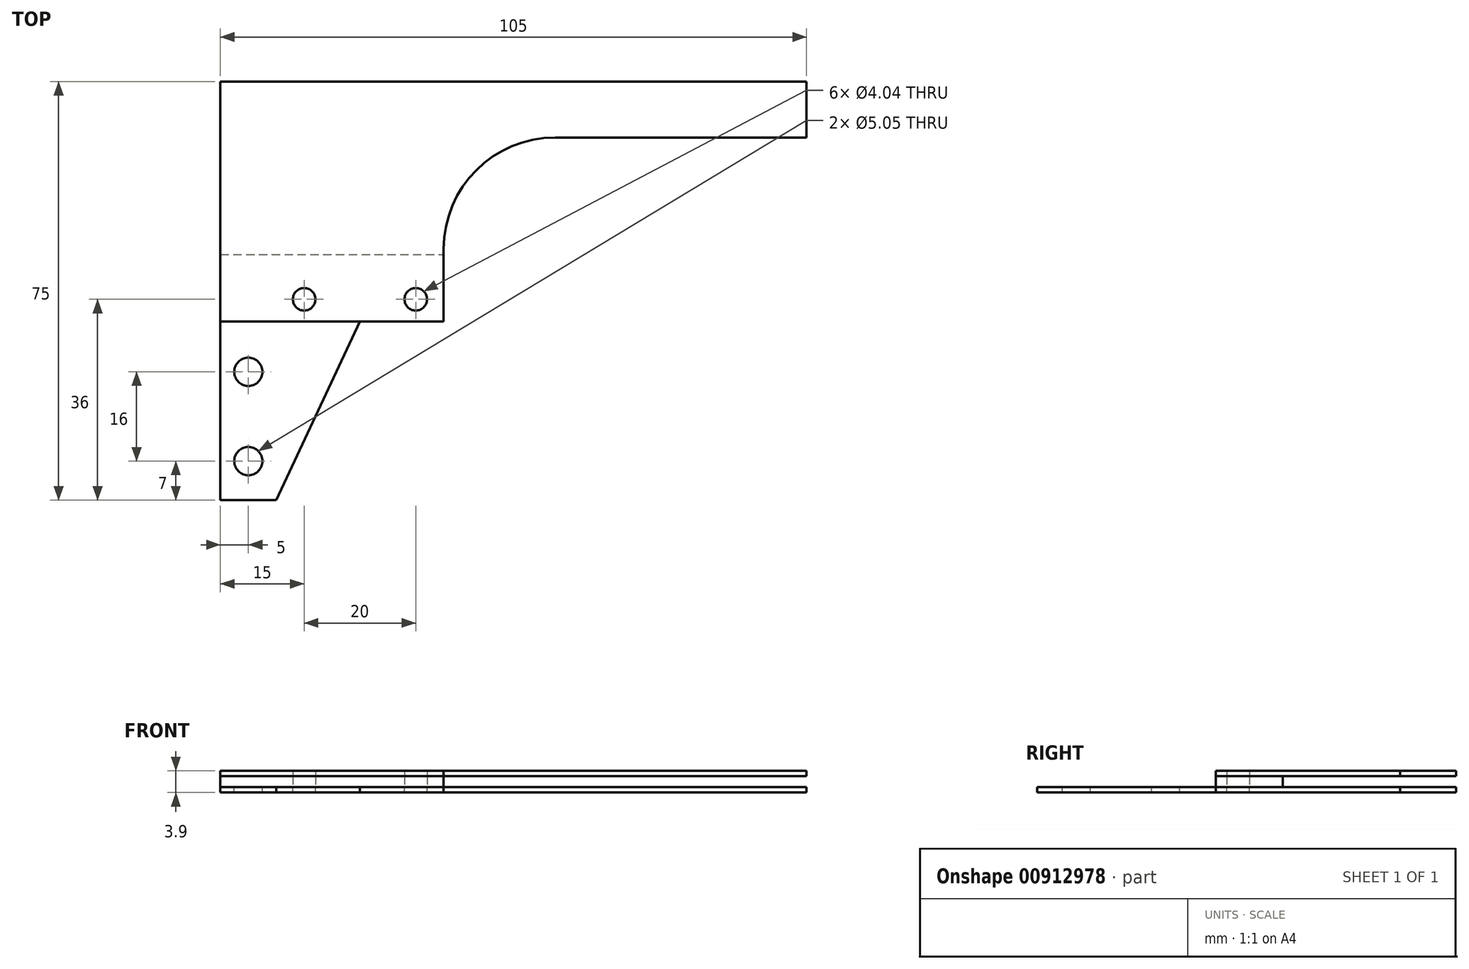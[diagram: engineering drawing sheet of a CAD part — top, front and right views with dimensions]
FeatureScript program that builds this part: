
annotation { "Feature Type Name" : "Feature", "Feature Type Description" : "" }
export const myFeature = defineFeature(function(context is Context, id is Id, definition is map)
    precondition{}
    {
        {
            assignVariable(context, id + "F0", {"name" : "G20", "anyValue" : .953});
        }
        {
            assignVariable(context, id + "F1", {"name" : "G2", "anyValue" : 2});
        }
        {
            var Q0;
            Q0=qCreatedBy(makeId("Top.planeOp"),FACE);
            var sketch = newSketch(context, id + "F2", { "sketchPlane" : qUnion([Q0])});
            skLineSegment(sketch, "E0.bottom", {"start": v(0, 0) * mm, "end": v(105, 0) * mm});
            skLineSegment(sketch, "E0.top", {"start": v(0, -75) * mm, "end": v(10, -75) * mm});
            skLineSegment(sketch, "E0.left", {"start": v(0, 0) * mm, "end": v(0, -75) * mm});
            skLineSegment(sketch, "E0.right", {"start": v(105, 0) * mm, "end": v(105, -10) * mm});
            skLineSegment(sketch, "E1", {"start": v(105, -10) * mm, "end": v(60, -10) * mm});
            skLineSegment(sketch, "E2", {"start": v(40, -30) * mm, "end": v(40, -43) * mm});
            skPoint(sketch, "E3.visualSharp", {"position": v(40, -10) * mm});
            skArc(sketch, "E3.filletArc", {"start": v(60, -10) * mm, "mid": v(45.86, -15.86) * mm, "end": v(40, -30) * mm});
            skCircle(sketch, "E4", {"center": v(5, -68) * mm, "radius": 2.53 * mm});
            skCircle(sketch, "E5", {"center": v(5, -52) * mm, "radius": 2.53 * mm});
            skLineSegment(sketch, "E6", {"start": v(40, -43) * mm, "end": v(25, -43) * mm});
            skLineSegment(sketch, "E7", {"start": v(25, -43) * mm, "end": v(10, -75) * mm});
            skCircle(sketch, "E8", {"center": v(35, -39) * mm, "radius": 2.02 * mm});
            skCircle(sketch, "E9", {"center": v(15, -39) * mm, "radius": 2.02 * mm});
            skLineSegment(sketch, "E10", {"start": v(25, -43) * mm, "end": v(0, -43) * mm});
            skLineSegment(sketch, "E11", {"start": v(0, -31) * mm, "end": v(40, -31) * mm});
            skSolve(sketch);
        }
        {
            var Q0;
            {var subQ2=sQuery(id+"F2.wireOp",EDGE,"E0.bottom");Q0=makeQuery(id+"F2.imprint","IMPRINT",FACE,{"disambiguationData":[TD([[makeQuery(id+"F2.imprint","IMPRINT",EDGE,{"derivedFrom":subQ2}),-1.0]])]});}
            var Q1;
            {var subQ3=sQuery(id+"F2.wireOp",EDGE,"E6");Q1=makeQuery(id+"F2.imprint","IMPRINT",FACE,{"disambiguationData":[TD([[makeQuery(id+"F2.imprint","IMPRINT",EDGE,{"derivedFrom":subQ3}),-1.0]])]});}
            var Q2;
            {var subQ1=sQuery(id+"F2.wireOp",EDGE,"E0.top");Q2=makeQuery(id+"F2.imprint","IMPRINT",FACE,{"disambiguationData":[TD([[makeQuery(id+"F2.imprint","IMPRINT",EDGE,{"derivedFrom":subQ1}),1.0]])]});}
            extrude(context, id + "F3", {"entities" : qUnion([Q0, Q1, Q2]), "oppositeDirection" : true, "depth" : (getVariable(context, 'G20')) * mm, "offsetDistance" : 25 * mm});
        }
        {
            var Q0;
            {var subQ2=sQuery(id+"F2.wireOp",EDGE,"E0.bottom");Q0=makeQuery(id+"F2.imprint","IMPRINT",FACE,{"disambiguationData":[TD([[makeQuery(id+"F2.imprint","IMPRINT",EDGE,{"derivedFrom":subQ2}),-1.0]])]});}
            var Q1;
            {var subQ3=sQuery(id+"F2.wireOp",EDGE,"E6");Q1=makeQuery(id+"F2.imprint","IMPRINT",FACE,{"disambiguationData":[TD([[makeQuery(id+"F2.imprint","IMPRINT",EDGE,{"derivedFrom":subQ3}),-1.0]])]});}
            extrude(context, id + "F4", {"entities" : qUnion([Q0, Q1]), "depth" : ((getVariable(context, 'G2')) + (getVariable(context, 'G20'))) * mm, "offsetDistance" : 25 * mm, "hasSecondDirection" : true, "secondDirectionOppositeDirection" : false, "secondDirectionDepth" : (getVariable(context, 'G2')) * mm});
        }
        {
            var Q0;
            {var subQ3=sQuery(id+"F2.wireOp",EDGE,"E6");Q0=makeQuery(id+"F2.imprint","IMPRINT",FACE,{"disambiguationData":[TD([[makeQuery(id+"F2.imprint","IMPRINT",EDGE,{"derivedFrom":subQ3}),-1.0]])]});}
            extrude(context, id + "F5", {"entities" : qUnion([Q0]), "depth" : (getVariable(context, 'G2')) * mm, "offsetDistance" : 25 * mm});
        }
    });
